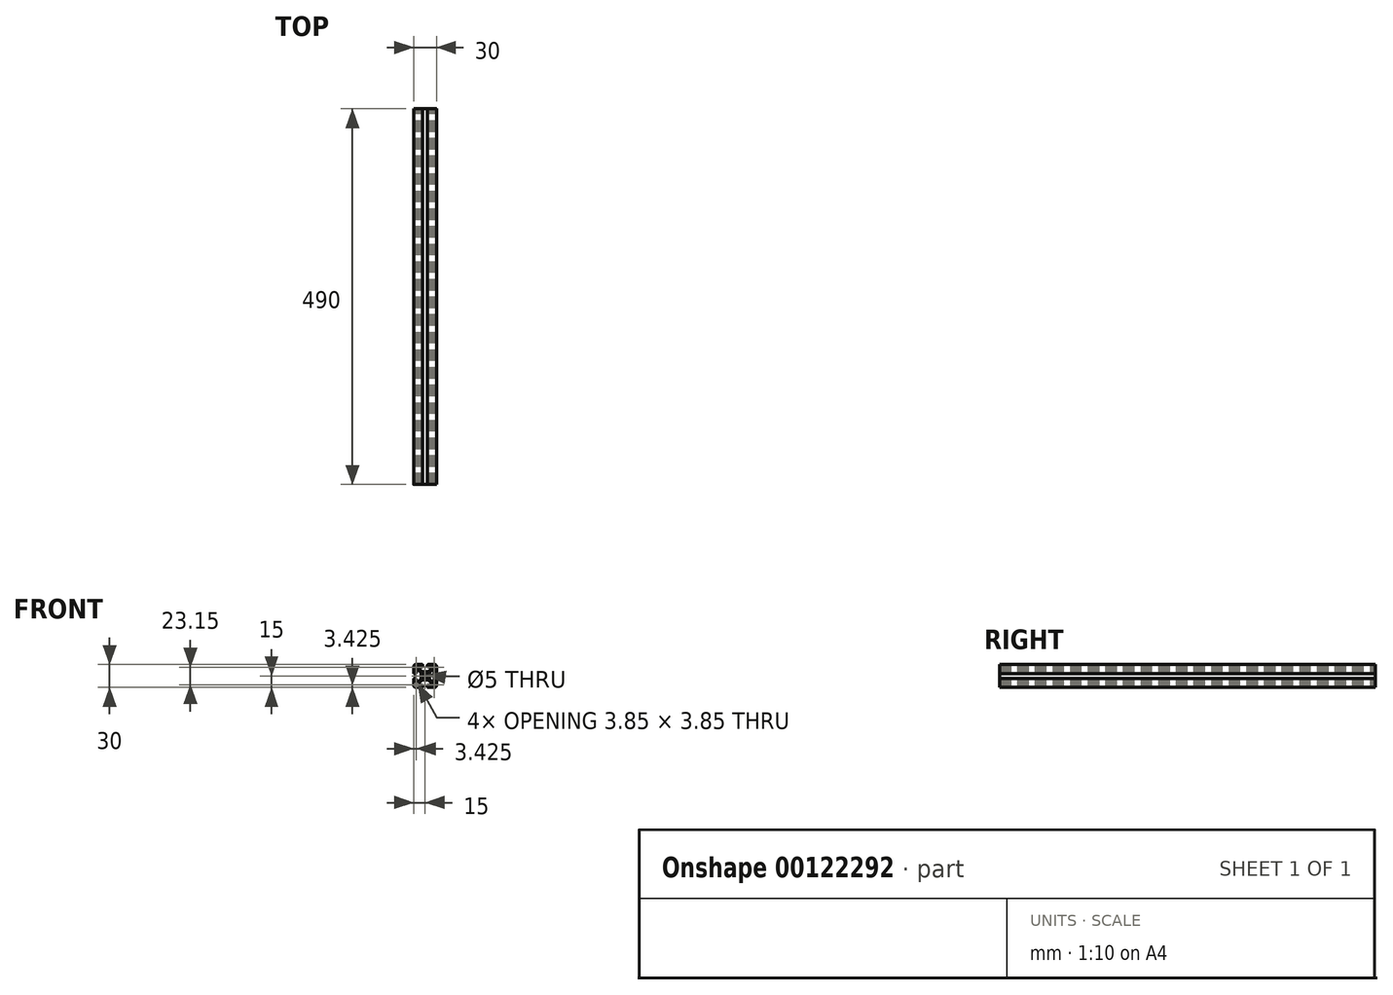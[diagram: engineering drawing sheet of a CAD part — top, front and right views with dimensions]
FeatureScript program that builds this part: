
annotation { "Feature Type Name" : "Feature", "Feature Type Description" : "" }
export const myFeature = defineFeature(function(context is Context, id is Id, definition is map)
    precondition{}
    {
        {
            var Q0;
            Q0=qCreatedBy(makeId("Front.planeOp"),FACE);
            var sketch = newSketch(context, id + "F0", { "sketchPlane" : qUnion([Q0])});
            skLineSegment(sketch, "E0", {"start": v(0, 5.25) * mm, "end": v(2.6, 5.25) * mm});
            skLineSegment(sketch, "E1", {"start": v(4.71, 6.13) * mm, "end": v(7.27, 8.69) * mm});
            skLineSegment(sketch, "E2", {"start": v(8.15, 10.8) * mm, "end": v(8.15, 12.5) * mm});
            skLineSegment(sketch, "E3", {"start": v(7.15, 13.5) * mm, "end": v(5.9, 13.5) * mm});
            skLineSegment(sketch, "E4", {"start": v(5.6, 13.2) * mm, "end": v(5.6, 12.3) * mm});
            skLineSegment(sketch, "E5", {"start": v(5.3, 12) * mm, "end": v(3.9, 12) * mm});
            skLineSegment(sketch, "E6", {"start": v(3.1, 12.8) * mm, "end": v(3.1, 14) * mm});
            skLineSegment(sketch, "E7", {"start": v(4.1, 15) * mm, "end": v(12, 15) * mm});
            skPoint(sketch, "E8.visualSharp", {"position": v(3.84, 5.25) * mm});
            skArc(sketch, "E8.filletArc", {"start": v(2.6, 5.25) * mm, "mid": v(3.74, 5.48) * mm, "end": v(4.71, 6.13) * mm});
            skPoint(sketch, "E9.visualSharp", {"position": v(8.15, 9.56) * mm});
            skArc(sketch, "E9.filletArc", {"start": v(7.27, 8.69) * mm, "mid": v(7.92, 9.66) * mm, "end": v(8.15, 10.8) * mm});
            skPoint(sketch, "E10.visualSharp", {"position": v(8.15, 13.5) * mm});
            skArc(sketch, "E10.filletArc", {"start": v(8.15, 12.5) * mm, "mid": v(7.86, 13.2) * mm, "end": v(7.15, 13.5) * mm});
            skPoint(sketch, "E11.visualSharp", {"position": v(5.6, 13.5) * mm});
            skArc(sketch, "E11.filletArc", {"start": v(5.9, 13.5) * mm, "mid": v(5.69, 13.41) * mm, "end": v(5.6, 13.2) * mm});
            skPoint(sketch, "E12.visualSharp", {"position": v(5.6, 12) * mm});
            skArc(sketch, "E12.filletArc", {"start": v(5.3, 12) * mm, "mid": v(5.51, 12.09) * mm, "end": v(5.6, 12.3) * mm});
            skPoint(sketch, "E13.visualSharp", {"position": v(3.1, 12) * mm});
            skArc(sketch, "E13.filletArc", {"start": v(3.1, 12.8) * mm, "mid": v(3.33, 12.23) * mm, "end": v(3.9, 12) * mm});
            skPoint(sketch, "E14.visualSharp", {"position": v(3.1, 15) * mm});
            skArc(sketch, "E14.filletArc", {"start": v(4.1, 15) * mm, "mid": v(3.4, 14.7) * mm, "end": v(3.1, 14) * mm});
            skArc(sketch, "E15.MirrorCS", {"start": v(12, 5.3) * mm, "mid": v(12.09, 5.51) * mm, "end": v(12.3, 5.6) * mm});
            skArc(sketch, "E16.MirrorCS", {"start": v(13.5, 5.9) * mm, "mid": v(13.41, 5.69) * mm, "end": v(13.2, 5.6) * mm});
            skPoint(sketch, "E17.MirrorP", {"position": v(13.5, 5.6) * mm});
            skLineSegment(sketch, "E18.MirrorCS", {"start": v(5.25, 0) * mm, "end": v(5.25, 2.6) * mm});
            skLineSegment(sketch, "E19.MirrorCS", {"start": v(6.13, 4.71) * mm, "end": v(8.69, 7.27) * mm});
            skPoint(sketch, "E20.MirrorP", {"position": v(13.5, 8.15) * mm});
            skLineSegment(sketch, "E21.MirrorCS", {"start": v(10.8, 8.15) * mm, "end": v(12.5, 8.15) * mm});
            skLineSegment(sketch, "E22.MirrorCS", {"start": v(13.5, 7.15) * mm, "end": v(13.5, 5.9) * mm});
            skPoint(sketch, "E23.MirrorP", {"position": v(9.56, 8.15) * mm});
            skLineSegment(sketch, "E24.MirrorCS", {"start": v(13.2, 5.6) * mm, "end": v(12.3, 5.6) * mm});
            skArc(sketch, "E25.MirrorCS", {"start": v(15, 4.1) * mm, "mid": v(14.7, 3.4) * mm, "end": v(14, 3.1) * mm});
            skArc(sketch, "E26.MirrorCS", {"start": v(12.8, 3.1) * mm, "mid": v(12.23, 3.33) * mm, "end": v(12, 3.9) * mm});
            skPoint(sketch, "E27.MirrorP", {"position": v(12, 5.6) * mm});
            skLineSegment(sketch, "E28.MirrorCS", {"start": v(12, 5.3) * mm, "end": v(12, 3.9) * mm});
            skPoint(sketch, "E29.MirrorP", {"position": v(5.25, 3.84) * mm});
            skLineSegment(sketch, "E30.MirrorCS", {"start": v(15, 4.1) * mm, "end": v(15, 12) * mm});
            skLineSegment(sketch, "E31.MirrorCS", {"start": v(12.8, 3.1) * mm, "end": v(14, 3.1) * mm});
            skArc(sketch, "E32.MirrorCS", {"start": v(5.25, 2.6) * mm, "mid": v(5.48, 3.74) * mm, "end": v(6.13, 4.71) * mm});
            skArc(sketch, "E33.MirrorCS", {"start": v(12.5, 8.15) * mm, "mid": v(13.2, 7.86) * mm, "end": v(13.5, 7.15) * mm});
            skArc(sketch, "E34.MirrorCS", {"start": v(8.69, 7.27) * mm, "mid": v(9.66, 7.92) * mm, "end": v(10.8, 8.15) * mm});
            skPoint(sketch, "E35.MirrorP", {"position": v(15, 3.1) * mm});
            skPoint(sketch, "E36.MirrorP", {"position": v(12, 3.1) * mm});
            skArc(sketch, "E37.MirrorCS", {"start": v(-5.9, 13.5) * mm, "mid": v(-5.69, 13.41) * mm, "end": v(-5.6, 13.2) * mm});
            skLineSegment(sketch, "E38.MirrorCS", {"start": v(-5.6, 13.2) * mm, "end": v(-5.6, 12.3) * mm});
            skArc(sketch, "E39.MirrorCS", {"start": v(-5.3, 12) * mm, "mid": v(-5.51, 12.09) * mm, "end": v(-5.6, 12.3) * mm});
            skArc(sketch, "E40.MirrorCS", {"start": v(-12, 5.3) * mm, "mid": v(-12.09, 5.51) * mm, "end": v(-12.3, 5.6) * mm});
            skLineSegment(sketch, "E41.MirrorCS", {"start": v(-13.2, 5.6) * mm, "end": v(-12.3, 5.6) * mm});
            skArc(sketch, "E42.MirrorCS", {"start": v(-13.5, 5.9) * mm, "mid": v(-13.41, 5.69) * mm, "end": v(-13.2, 5.6) * mm});
            skArc(sketch, "E43.MirrorCS", {"start": v(-12.5, 8.15) * mm, "mid": v(-13.2, 7.86) * mm, "end": v(-13.5, 7.15) * mm});
            skArc(sketch, "E44.MirrorCS", {"start": v(-15, 4.1) * mm, "mid": v(-14.7, 3.4) * mm, "end": v(-14, 3.1) * mm});
            skArc(sketch, "E45.MirrorCS", {"start": v(-8.15, 12.5) * mm, "mid": v(-7.86, 13.2) * mm, "end": v(-7.15, 13.5) * mm});
            skLineSegment(sketch, "E46.MirrorCS", {"start": v(-5.3, 12) * mm, "end": v(-3.9, 12) * mm});
            skLineSegment(sketch, "E47.MirrorCS", {"start": v(-7.15, 13.5) * mm, "end": v(-5.9, 13.5) * mm});
            skArc(sketch, "E48.MirrorCS", {"start": v(-3.1, 12.8) * mm, "mid": v(-3.33, 12.23) * mm, "end": v(-3.9, 12) * mm});
            skArc(sketch, "E49.MirrorCS", {"start": v(-4.1, 15) * mm, "mid": v(-3.4, 14.7) * mm, "end": v(-3.1, 14) * mm});
            skArc(sketch, "E50.MirrorCS", {"start": v(-12.8, 3.1) * mm, "mid": v(-12.23, 3.33) * mm, "end": v(-12, 3.9) * mm});
            skPoint(sketch, "E51.MirrorP", {"position": v(-12, 3.1) * mm});
            skLineSegment(sketch, "E52.MirrorCS", {"start": v(-5.25, 0) * mm, "end": v(-5.25, 2.6) * mm});
            skLineSegment(sketch, "E53.MirrorCS", {"start": v(-10.8, 8.15) * mm, "end": v(-12.5, 8.15) * mm});
            skPoint(sketch, "E54.MirrorP", {"position": v(-9.56, 8.15) * mm});
            skLineSegment(sketch, "E55.MirrorCS", {"start": v(-12, 5.3) * mm, "end": v(-12, 3.9) * mm});
            skLineSegment(sketch, "E56.MirrorCS", {"start": v(-12.8, 3.1) * mm, "end": v(-14, 3.1) * mm});
            skArc(sketch, "E57.MirrorCS", {"start": v(-7.27, 8.69) * mm, "mid": v(-7.92, 9.66) * mm, "end": v(-8.15, 10.8) * mm});
            skArc(sketch, "E58.MirrorCS", {"start": v(-2.6, 5.25) * mm, "mid": v(-3.74, 5.48) * mm, "end": v(-4.71, 6.13) * mm});
            skLineSegment(sketch, "E59.MirrorCS", {"start": v(-4.1, 15) * mm, "end": v(-12, 15) * mm});
            skLineSegment(sketch, "E60.MirrorCS", {"start": v(-3.1, 12.8) * mm, "end": v(-3.1, 14) * mm});
            skPoint(sketch, "E61.MirrorP", {"position": v(-8.15, 9.56) * mm});
            skPoint(sketch, "E62.MirrorP", {"position": v(-8.15, 13.5) * mm});
            skPoint(sketch, "E63.MirrorP", {"position": v(-5.25, 3.84) * mm});
            skLineSegment(sketch, "E64.MirrorCS", {"start": v(-8.15, 10.8) * mm, "end": v(-8.15, 12.5) * mm});
            skPoint(sketch, "E65.MirrorP", {"position": v(-15, 3.1) * mm});
            skPoint(sketch, "E66.MirrorP", {"position": v(-5.6, 13.5) * mm});
            skPoint(sketch, "E67.MirrorP", {"position": v(-3.1, 15) * mm});
            skLineSegment(sketch, "E68.MirrorCS", {"start": v(-6.13, 4.71) * mm, "end": v(-8.69, 7.27) * mm});
            skLineSegment(sketch, "E69.MirrorCS", {"start": v(-4.71, 6.13) * mm, "end": v(-7.27, 8.69) * mm});
            skArc(sketch, "E70.MirrorCS", {"start": v(-8.69, 7.27) * mm, "mid": v(-9.66, 7.92) * mm, "end": v(-10.8, 8.15) * mm});
            skLineSegment(sketch, "E71.MirrorCS", {"start": v(-13.5, 7.15) * mm, "end": v(-13.5, 5.9) * mm});
            skPoint(sketch, "E72.MirrorP", {"position": v(-13.5, 8.15) * mm});
            skPoint(sketch, "E73.MirrorP", {"position": v(-3.1, 12) * mm});
            skPoint(sketch, "E74.MirrorP", {"position": v(-3.84, 5.25) * mm});
            skPoint(sketch, "E75.MirrorP", {"position": v(-5.6, 12) * mm});
            skLineSegment(sketch, "E76.MirrorCS", {"start": v(0, 5.25) * mm, "end": v(-2.6, 5.25) * mm});
            skLineSegment(sketch, "E77.MirrorCS", {"start": v(-15, 4.1) * mm, "end": v(-15, 12) * mm});
            skArc(sketch, "E78.MirrorCS", {"start": v(-5.25, 2.6) * mm, "mid": v(-5.48, 3.74) * mm, "end": v(-6.13, 4.71) * mm});
            skPoint(sketch, "E79.MirrorP", {"position": v(-12, 5.6) * mm});
            skPoint(sketch, "E80.MirrorP", {"position": v(-13.5, 5.6) * mm});
            skLineSegment(sketch, "E81.MirrorCS", {"start": v(5.6, -13.2) * mm, "end": v(5.6, -12.3) * mm});
            skArc(sketch, "E82.MirrorCS", {"start": v(5.9, -13.5) * mm, "mid": v(5.69, -13.41) * mm, "end": v(5.6, -13.2) * mm});
            skArc(sketch, "E83.MirrorCS", {"start": v(5.3, -12) * mm, "mid": v(5.51, -12.09) * mm, "end": v(5.6, -12.3) * mm});
            skArc(sketch, "E84.MirrorCS", {"start": v(-12, -5.3) * mm, "mid": v(-12.09, -5.51) * mm, "end": v(-12.3, -5.6) * mm});
            skArc(sketch, "E85.MirrorCS", {"start": v(-5.9, -13.5) * mm, "mid": v(-5.69, -13.41) * mm, "end": v(-5.6, -13.2) * mm});
            skLineSegment(sketch, "E86.MirrorCS", {"start": v(13.2, -5.6) * mm, "end": v(12.3, -5.6) * mm});
            skArc(sketch, "E87.MirrorCS", {"start": v(-5.3, -12) * mm, "mid": v(-5.51, -12.09) * mm, "end": v(-5.6, -12.3) * mm});
            skArc(sketch, "E88.MirrorCS", {"start": v(13.5, -5.9) * mm, "mid": v(13.41, -5.69) * mm, "end": v(13.2, -5.6) * mm});
            skLineSegment(sketch, "E89.MirrorCS", {"start": v(-5.6, -13.2) * mm, "end": v(-5.6, -12.3) * mm});
            skArc(sketch, "E90.MirrorCS", {"start": v(-13.5, -5.9) * mm, "mid": v(-13.41, -5.69) * mm, "end": v(-13.2, -5.6) * mm});
            skArc(sketch, "E91.MirrorCS", {"start": v(12, -5.3) * mm, "mid": v(12.09, -5.51) * mm, "end": v(12.3, -5.6) * mm});
            skLineSegment(sketch, "E92.MirrorCS", {"start": v(-13.2, -5.6) * mm, "end": v(-12.3, -5.6) * mm});
            skArc(sketch, "E93.MirrorCS", {"start": v(-15, -4.1) * mm, "mid": v(-14.7, -3.4) * mm, "end": v(-14, -3.1) * mm});
            skArc(sketch, "E94.MirrorCS", {"start": v(-12.5, -8.15) * mm, "mid": v(-13.2, -7.86) * mm, "end": v(-13.5, -7.15) * mm});
            skArc(sketch, "E95.MirrorCS", {"start": v(12.8, -3.1) * mm, "mid": v(12.23, -3.33) * mm, "end": v(12, -3.9) * mm});
            skArc(sketch, "E96.MirrorCS", {"start": v(-12.8, -3.1) * mm, "mid": v(-12.23, -3.33) * mm, "end": v(-12, -3.9) * mm});
            skLineSegment(sketch, "E97.MirrorCS", {"start": v(7.15, -13.5) * mm, "end": v(5.9, -13.5) * mm});
            skLineSegment(sketch, "E98.MirrorCS", {"start": v(5.3, -12) * mm, "end": v(3.9, -12) * mm});
            skArc(sketch, "E99.MirrorCS", {"start": v(8.15, -12.5) * mm, "mid": v(7.86, -13.2) * mm, "end": v(7.15, -13.5) * mm});
            skArc(sketch, "E100.MirrorCS", {"start": v(-4.1, -15) * mm, "mid": v(-3.4, -14.7) * mm, "end": v(-3.1, -14) * mm});
            skArc(sketch, "E101.MirrorCS", {"start": v(-3.1, -12.8) * mm, "mid": v(-3.33, -12.23) * mm, "end": v(-3.9, -12) * mm});
            skArc(sketch, "E102.MirrorCS", {"start": v(15, -4.1) * mm, "mid": v(14.7, -3.4) * mm, "end": v(14, -3.1) * mm});
            skArc(sketch, "E103.MirrorCS", {"start": v(-8.15, -12.5) * mm, "mid": v(-7.86, -13.2) * mm, "end": v(-7.15, -13.5) * mm});
            skArc(sketch, "E104.MirrorCS", {"start": v(12.5, -8.15) * mm, "mid": v(13.2, -7.86) * mm, "end": v(13.5, -7.15) * mm});
            skArc(sketch, "E105.MirrorCS", {"start": v(3.1, -12.8) * mm, "mid": v(3.33, -12.23) * mm, "end": v(3.9, -12) * mm});
            skArc(sketch, "E106.MirrorCS", {"start": v(4.1, -15) * mm, "mid": v(3.4, -14.7) * mm, "end": v(3.1, -14) * mm});
            skPoint(sketch, "E107.MirrorP", {"position": v(-3.1, -15) * mm});
            skArc(sketch, "E108.MirrorCS", {"start": v(-2.6, -5.25) * mm, "mid": v(-3.74, -5.48) * mm, "end": v(-4.71, -6.13) * mm});
            skLineSegment(sketch, "E109.MirrorCS", {"start": v(5.25, 0) * mm, "end": v(5.25, -2.6) * mm});
            skLineSegment(sketch, "E110.MirrorCS", {"start": v(-6.13, -4.71) * mm, "end": v(-8.69, -7.27) * mm});
            skLineSegment(sketch, "E111.MirrorCS", {"start": v(-12, -5.3) * mm, "end": v(-12, -3.9) * mm});
            skLineSegment(sketch, "E112.MirrorCS", {"start": v(12, -5.3) * mm, "end": v(12, -3.9) * mm});
            skLineSegment(sketch, "E113.MirrorCS", {"start": v(-7.15, -13.5) * mm, "end": v(-5.9, -13.5) * mm});
            skLineSegment(sketch, "E114.MirrorCS", {"start": v(-13.5, -7.15) * mm, "end": v(-13.5, -5.9) * mm});
            skPoint(sketch, "E115.MirrorP", {"position": v(5.6, -12) * mm});
            skPoint(sketch, "E116.MirrorP", {"position": v(12, -5.6) * mm});
            skPoint(sketch, "E117.MirrorP", {"position": v(-5.25, -3.84) * mm});
            skPoint(sketch, "E118.MirrorP", {"position": v(3.1, -15) * mm});
            skPoint(sketch, "E119.MirrorP", {"position": v(-5.6, -13.5) * mm});
            skArc(sketch, "E120.MirrorCS", {"start": v(-7.27, -8.69) * mm, "mid": v(-7.92, -9.66) * mm, "end": v(-8.15, -10.8) * mm});
            skPoint(sketch, "E121.MirrorP", {"position": v(8.15, -9.56) * mm});
            skPoint(sketch, "E122.MirrorP", {"position": v(9.56, -8.15) * mm});
            skPoint(sketch, "E123.MirrorP", {"position": v(-3.1, -12) * mm});
            skArc(sketch, "E124.MirrorCS", {"start": v(8.69, -7.27) * mm, "mid": v(9.66, -7.92) * mm, "end": v(10.8, -8.15) * mm});
            skLineSegment(sketch, "E125.MirrorCS", {"start": v(-8.15, -10.8) * mm, "end": v(-8.15, -12.5) * mm});
            skLineSegment(sketch, "E126.MirrorCS", {"start": v(-10.8, -8.15) * mm, "end": v(-12.5, -8.15) * mm});
            skLineSegment(sketch, "E127.MirrorCS", {"start": v(13.5, -7.15) * mm, "end": v(13.5, -5.9) * mm});
            skPoint(sketch, "E128.MirrorP", {"position": v(-9.56, -8.15) * mm});
            skPoint(sketch, "E129.MirrorP", {"position": v(-13.5, -5.6) * mm});
            skLineSegment(sketch, "E130.MirrorCS", {"start": v(-5.3, -12) * mm, "end": v(-3.9, -12) * mm});
            skArc(sketch, "E131.MirrorCS", {"start": v(-8.69, -7.27) * mm, "mid": v(-9.66, -7.92) * mm, "end": v(-10.8, -8.15) * mm});
            skArc(sketch, "E132.MirrorCS", {"start": v(5.25, -2.6) * mm, "mid": v(5.48, -3.74) * mm, "end": v(6.13, -4.71) * mm});
            skArc(sketch, "E133.MirrorCS", {"start": v(-5.25, -2.6) * mm, "mid": v(-5.48, -3.74) * mm, "end": v(-6.13, -4.71) * mm});
            skPoint(sketch, "E134.MirrorP", {"position": v(12, -3.1) * mm});
            skPoint(sketch, "E135.MirrorP", {"position": v(-8.15, -13.5) * mm});
            skPoint(sketch, "E136.MirrorP", {"position": v(-5.6, -12) * mm});
            skPoint(sketch, "E137.MirrorP", {"position": v(8.15, -13.5) * mm});
            skPoint(sketch, "E138.MirrorP", {"position": v(-3.84, -5.25) * mm});
            skPoint(sketch, "E139.MirrorP", {"position": v(-8.15, -9.56) * mm});
            skPoint(sketch, "E140.MirrorP", {"position": v(15, -3.1) * mm});
            skLineSegment(sketch, "E141.MirrorCS", {"start": v(3.1, -12.8) * mm, "end": v(3.1, -14) * mm});
            skLineSegment(sketch, "E142.MirrorCS", {"start": v(4.1, -15) * mm, "end": v(12, -15) * mm});
            skArc(sketch, "E143.MirrorCS", {"start": v(2.6, -5.25) * mm, "mid": v(3.74, -5.48) * mm, "end": v(4.71, -6.13) * mm});
            skArc(sketch, "E144.MirrorCS", {"start": v(7.27, -8.69) * mm, "mid": v(7.92, -9.66) * mm, "end": v(8.15, -10.8) * mm});
            skPoint(sketch, "E145.MirrorP", {"position": v(-15, -3.1) * mm});
            skLineSegment(sketch, "E146.MirrorCS", {"start": v(-15, -4.1) * mm, "end": v(-15, -12) * mm});
            skLineSegment(sketch, "E147.MirrorCS", {"start": v(0, -5.25) * mm, "end": v(-2.6, -5.25) * mm});
            skLineSegment(sketch, "E148.MirrorCS", {"start": v(15, -4.1) * mm, "end": v(15, -12) * mm});
            skLineSegment(sketch, "E149.MirrorCS", {"start": v(12.8, -3.1) * mm, "end": v(14, -3.1) * mm});
            skLineSegment(sketch, "E150.MirrorCS", {"start": v(-4.71, -6.13) * mm, "end": v(-7.27, -8.69) * mm});
            skPoint(sketch, "E151.MirrorP", {"position": v(5.6, -13.5) * mm});
            skPoint(sketch, "E152.MirrorP", {"position": v(-12, -5.6) * mm});
            skPoint(sketch, "E153.MirrorP", {"position": v(5.25, -3.84) * mm});
            skPoint(sketch, "E154.MirrorP", {"position": v(-12, -3.1) * mm});
            skLineSegment(sketch, "E155.MirrorCS", {"start": v(10.8, -8.15) * mm, "end": v(12.5, -8.15) * mm});
            skPoint(sketch, "E156.MirrorP", {"position": v(3.84, -5.25) * mm});
            skPoint(sketch, "E157.MirrorP", {"position": v(13.5, -5.6) * mm});
            skPoint(sketch, "E158.MirrorP", {"position": v(-13.5, -8.15) * mm});
            skPoint(sketch, "E159.MirrorP", {"position": v(13.5, -8.15) * mm});
            skLineSegment(sketch, "E160.MirrorCS", {"start": v(0, -5.25) * mm, "end": v(2.6, -5.25) * mm});
            skLineSegment(sketch, "E161.MirrorCS", {"start": v(6.13, -4.71) * mm, "end": v(8.69, -7.27) * mm});
            skLineSegment(sketch, "E162.MirrorCS", {"start": v(-3.1, -12.8) * mm, "end": v(-3.1, -14) * mm});
            skLineSegment(sketch, "E163.MirrorCS", {"start": v(-5.25, 0) * mm, "end": v(-5.25, -2.6) * mm});
            skLineSegment(sketch, "E164.MirrorCS", {"start": v(-4.1, -15) * mm, "end": v(-12, -15) * mm});
            skLineSegment(sketch, "E165.MirrorCS", {"start": v(4.71, -6.13) * mm, "end": v(7.27, -8.69) * mm});
            skLineSegment(sketch, "E166.MirrorCS", {"start": v(-12.8, -3.1) * mm, "end": v(-14, -3.1) * mm});
            skLineSegment(sketch, "E167.MirrorCS", {"start": v(8.15, -10.8) * mm, "end": v(8.15, -12.5) * mm});
            skPoint(sketch, "E168.MirrorP", {"position": v(3.1, -12) * mm});
            skCircle(sketch, "E169", {"center": v(0, 0) * mm, "radius": 2.5 * mm});
            skLineSegment(sketch, "E170.bottom", {"start": v(9.95, 13.5) * mm, "end": v(12, 13.5) * mm});
            skLineSegment(sketch, "E170.top", {"start": v(9.95, 9.65) * mm, "end": v(13.2, 9.65) * mm});
            skLineSegment(sketch, "E170.left", {"start": v(9.65, 13.2) * mm, "end": v(9.65, 9.95) * mm});
            skLineSegment(sketch, "E170.right", {"start": v(13.5, 12) * mm, "end": v(13.5, 9.95) * mm});
            skPoint(sketch, "E171.visualSharp", {"position": v(9.65, 9.65) * mm});
            skArc(sketch, "E171.filletArc", {"start": v(9.65, 9.95) * mm, "mid": v(9.74, 9.74) * mm, "end": v(9.95, 9.65) * mm});
            skPoint(sketch, "E172.visualSharp", {"position": v(13.5, 9.65) * mm});
            skArc(sketch, "E172.filletArc", {"start": v(13.2, 9.65) * mm, "mid": v(13.41, 9.74) * mm, "end": v(13.5, 9.95) * mm});
            skPoint(sketch, "E173.visualSharp", {"position": v(9.65, 13.5) * mm});
            skArc(sketch, "E173.filletArc", {"start": v(9.95, 13.5) * mm, "mid": v(9.74, 13.41) * mm, "end": v(9.65, 13.2) * mm});
            skPoint(sketch, "E174.visualSharp", {"position": v(13.5, 13.5) * mm});
            skArc(sketch, "E174.filletArc", {"start": v(13.5, 12) * mm, "mid": v(13.06, 13.06) * mm, "end": v(12, 13.5) * mm});
            skArc(sketch, "E175.MirrorCS", {"start": v(-13.2, 9.65) * mm, "mid": v(-13.41, 9.74) * mm, "end": v(-13.5, 9.95) * mm});
            skArc(sketch, "E176.MirrorCS", {"start": v(-9.65, 9.95) * mm, "mid": v(-9.74, 9.74) * mm, "end": v(-9.95, 9.65) * mm});
            skArc(sketch, "E177.MirrorCS", {"start": v(-9.95, 13.5) * mm, "mid": v(-9.74, 13.41) * mm, "end": v(-9.65, 13.2) * mm});
            skPoint(sketch, "E178.MirrorP", {"position": v(-13.5, 9.65) * mm});
            skPoint(sketch, "E179.MirrorP", {"position": v(-9.65, 9.65) * mm});
            skArc(sketch, "E180.MirrorCS", {"start": v(-13.5, 12) * mm, "mid": v(-13.06, 13.06) * mm, "end": v(-12, 13.5) * mm});
            skLineSegment(sketch, "E181.MirrorCS", {"start": v(-13.5, 12) * mm, "end": v(-13.5, 9.95) * mm});
            skLineSegment(sketch, "E182.MirrorCS", {"start": v(-9.95, 13.5) * mm, "end": v(-12, 13.5) * mm});
            skPoint(sketch, "E183.MirrorP", {"position": v(-13.5, 13.5) * mm});
            skPoint(sketch, "E184.MirrorP", {"position": v(-9.65, 13.5) * mm});
            skLineSegment(sketch, "E185.MirrorCS", {"start": v(-9.95, 9.65) * mm, "end": v(-13.2, 9.65) * mm});
            skLineSegment(sketch, "E186.MirrorCS", {"start": v(-9.65, 13.2) * mm, "end": v(-9.65, 9.95) * mm});
            skArc(sketch, "E187.MirrorCS", {"start": v(-9.65, -9.95) * mm, "mid": v(-9.74, -9.74) * mm, "end": v(-9.95, -9.65) * mm});
            skArc(sketch, "E188.MirrorCS", {"start": v(-9.95, -13.5) * mm, "mid": v(-9.74, -13.41) * mm, "end": v(-9.65, -13.2) * mm});
            skArc(sketch, "E189.MirrorCS", {"start": v(-13.2, -9.65) * mm, "mid": v(-13.41, -9.74) * mm, "end": v(-13.5, -9.95) * mm});
            skArc(sketch, "E190.MirrorCS", {"start": v(-13.5, -12) * mm, "mid": v(-13.06, -13.06) * mm, "end": v(-12, -13.5) * mm});
            skLineSegment(sketch, "E191.MirrorCS", {"start": v(-13.5, -12) * mm, "end": v(-13.5, -9.95) * mm});
            skLineSegment(sketch, "E192.MirrorCS", {"start": v(-9.95, -13.5) * mm, "end": v(-12, -13.5) * mm});
            skLineSegment(sketch, "E193.MirrorCS", {"start": v(-9.95, -9.65) * mm, "end": v(-13.2, -9.65) * mm});
            skLineSegment(sketch, "E194.MirrorCS", {"start": v(-9.65, -13.2) * mm, "end": v(-9.65, -9.95) * mm});
            skPoint(sketch, "E195.MirrorP", {"position": v(-9.65, -13.5) * mm});
            skPoint(sketch, "E196.MirrorP", {"position": v(-13.5, -13.5) * mm});
            skPoint(sketch, "E197.MirrorP", {"position": v(-9.65, -9.65) * mm});
            skPoint(sketch, "E198.MirrorP", {"position": v(-13.5, -9.65) * mm});
            skArc(sketch, "E199.MirrorCS", {"start": v(9.95, -13.5) * mm, "mid": v(9.74, -13.41) * mm, "end": v(9.65, -13.2) * mm});
            skArc(sketch, "E200.MirrorCS", {"start": v(9.65, -9.95) * mm, "mid": v(9.74, -9.74) * mm, "end": v(9.95, -9.65) * mm});
            skArc(sketch, "E201.MirrorCS", {"start": v(13.2, -9.65) * mm, "mid": v(13.41, -9.74) * mm, "end": v(13.5, -9.95) * mm});
            skPoint(sketch, "E202.MirrorP", {"position": v(9.65, -13.5) * mm});
            skPoint(sketch, "E203.MirrorP", {"position": v(9.65, -9.65) * mm});
            skPoint(sketch, "E204.MirrorP", {"position": v(13.5, -9.65) * mm});
            skPoint(sketch, "E205.MirrorP", {"position": v(13.5, -13.5) * mm});
            skLineSegment(sketch, "E206.MirrorCS", {"start": v(9.95, -13.5) * mm, "end": v(12, -13.5) * mm});
            skLineSegment(sketch, "E207.MirrorCS", {"start": v(9.95, -9.65) * mm, "end": v(13.2, -9.65) * mm});
            skLineSegment(sketch, "E208.MirrorCS", {"start": v(13.5, -12) * mm, "end": v(13.5, -9.95) * mm});
            skLineSegment(sketch, "E209.MirrorCS", {"start": v(9.65, -13.2) * mm, "end": v(9.65, -9.95) * mm});
            skArc(sketch, "E210.MirrorCS", {"start": v(13.5, -12) * mm, "mid": v(13.06, -13.06) * mm, "end": v(12, -13.5) * mm});
            skPoint(sketch, "E211.visualSharp", {"position": v(15, 15) * mm});
            skArc(sketch, "E211.filletArc", {"start": v(15, 12) * mm, "mid": v(14.12, 14.12) * mm, "end": v(12, 15) * mm});
            skPoint(sketch, "E212.visualSharp", {"position": v(15, -15) * mm});
            skArc(sketch, "E212.filletArc", {"start": v(12, -15) * mm, "mid": v(14.12, -14.12) * mm, "end": v(15, -12) * mm});
            skPoint(sketch, "E213.visualSharp", {"position": v(-15, -15) * mm});
            skArc(sketch, "E213.filletArc", {"start": v(-15, -12) * mm, "mid": v(-14.12, -14.12) * mm, "end": v(-12, -15) * mm});
            skPoint(sketch, "E214.visualSharp", {"position": v(-15, 15) * mm});
            skArc(sketch, "E214.filletArc", {"start": v(-12, 15) * mm, "mid": v(-14.12, 14.12) * mm, "end": v(-15, 12) * mm});
            skSolve(sketch);
        }
        {
            var Q0;
            Q0 = qSketchRegion(id + "F0", true);
            extrude(context, id + "F1", {"entities" : qUnion([Q0]), "depth" : 490 * mm});
        }
    });
